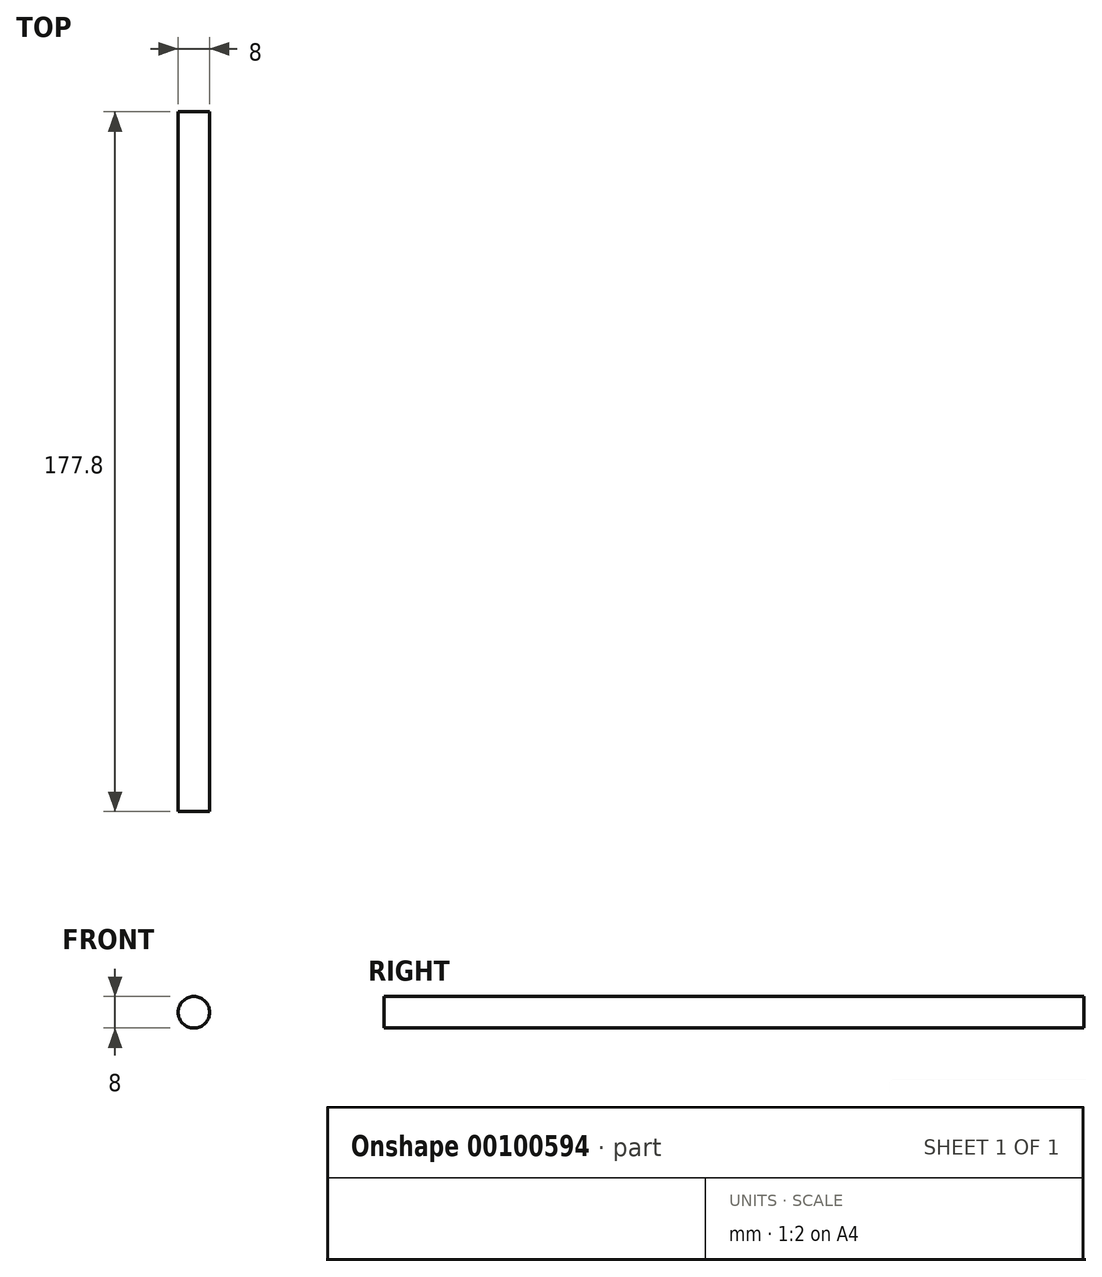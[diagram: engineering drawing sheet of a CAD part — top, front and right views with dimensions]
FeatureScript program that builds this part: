
annotation { "Feature Type Name" : "Feature", "Feature Type Description" : "" }
export const myFeature = defineFeature(function(context is Context, id is Id, definition is map)
    precondition{}
    {
        {
            var Q0;
            Q0=qCreatedBy(makeId("Front.planeOp"),FACE);
            var sketch = newSketch(context, id + "F0", { "sketchPlane" : qUnion([Q0])});
            skCircle(sketch, "E0", {"center": v(0, 0) * mm, "radius": 4 * mm});
            skSolve(sketch);
        }
        {
            var Q0;
            Q0=makeQuery(id+"F0.imprint","IMPRINT",FACE,{"disambiguationData":[TD([[makeQuery(id+"F0.imprint","IMPRINT",EDGE,{"derivedFrom":sQuery(id+"F0.wireOp",EDGE,"E0")}),1.0]])]});
            extrude(context, id + "F1", {"entities" : qUnion([Q0]), "depth" : 177.8 * mm});
        }
    });
